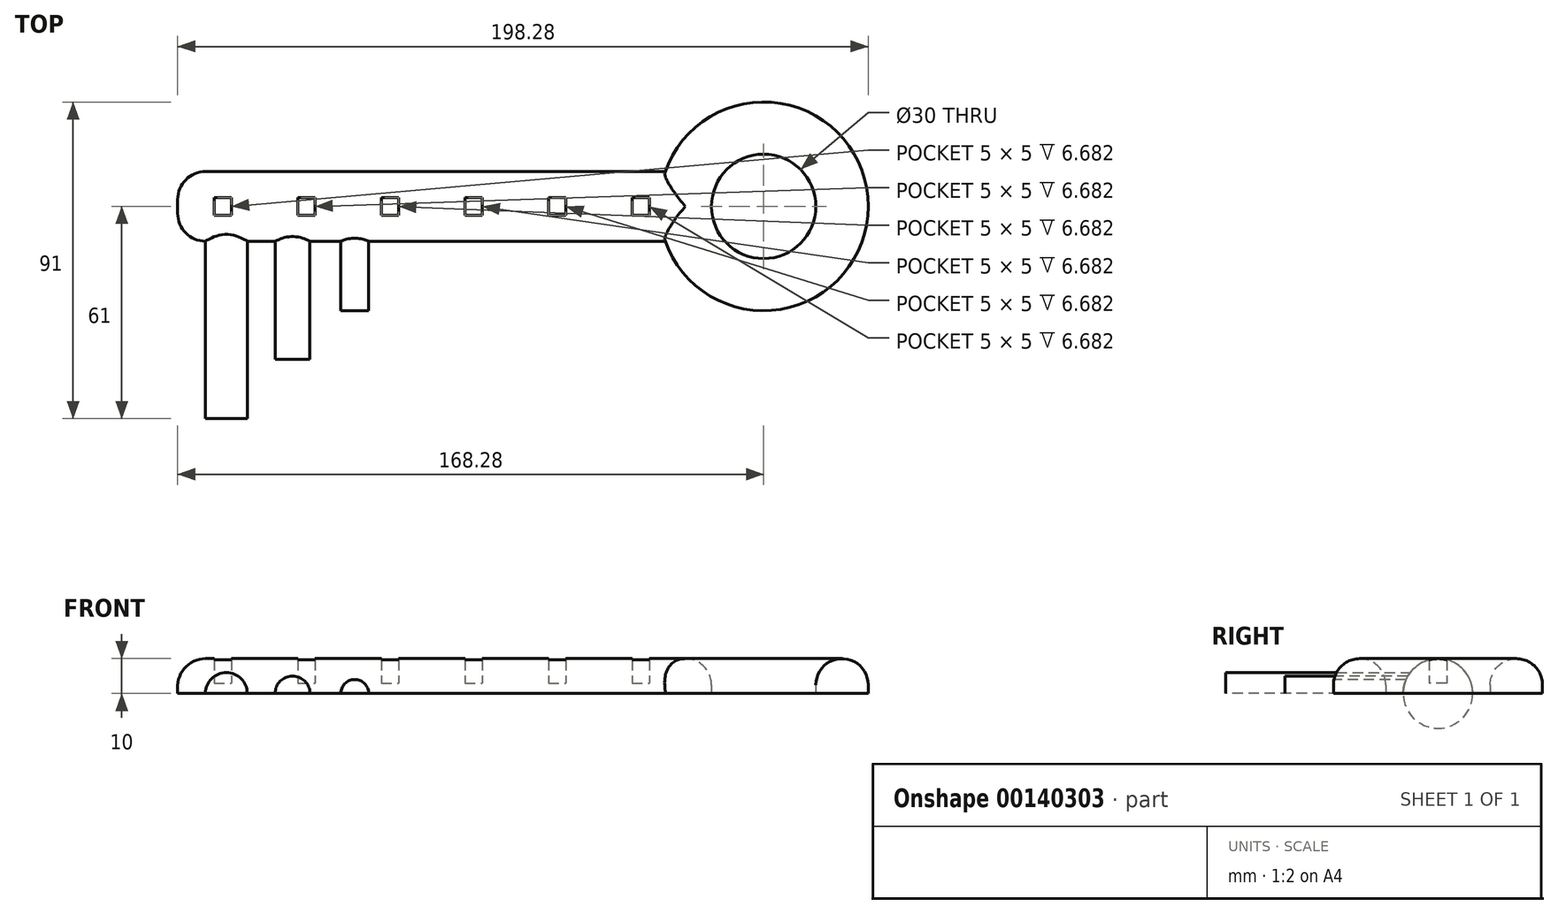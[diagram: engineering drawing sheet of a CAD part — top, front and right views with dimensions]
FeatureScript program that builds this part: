
annotation { "Feature Type Name" : "Feature", "Feature Type Description" : "" }
export const myFeature = defineFeature(function(context is Context, id is Id, definition is map)
    precondition{}
    {
        {
            var Q0;
            Q0=qCreatedBy(makeId("Top.planeOp"),FACE);
            var sketch = newSketch(context, id + "F0", { "sketchPlane" : qUnion([Q0])});
            skCircle(sketch, "E0", {"center": v(155.3, 0) * mm, "radius": 15 * mm});
            skCircle(sketch, "E1", {"center": v(155.3, 0) * mm, "radius": 30 * mm});
            skLineSegment(sketch, "E2", {"start": v(127.02, 10) * mm, "end": v(-12.98, 10) * mm});
            skLineSegment(sketch, "E3", {"start": v(-12.98, 10) * mm, "end": v(-12.98, -10) * mm});
            skPoint(sketch, "E4.first.point", {"position": v(185.3, 0) * mm});
            skLineSegment(sketch, "E5.bottom", {"start": v(-4.98, -10) * mm, "end": v(7.02, -10) * mm});
            skLineSegment(sketch, "E5.top", {"start": v(-4.98, -61) * mm, "end": v(7.02, -61) * mm});
            skLineSegment(sketch, "E5.left", {"start": v(-4.98, -10) * mm, "end": v(-4.98, -61) * mm});
            skLineSegment(sketch, "E5.right", {"start": v(7.02, -10) * mm, "end": v(7.02, -61) * mm});
            skLineSegment(sketch, "E6.bottom", {"start": v(15.02, -10) * mm, "end": v(25.02, -10) * mm});
            skLineSegment(sketch, "E6.top", {"start": v(15.02, -44) * mm, "end": v(25.02, -44) * mm});
            skLineSegment(sketch, "E6.left", {"start": v(15.02, -10) * mm, "end": v(15.02, -44) * mm});
            skLineSegment(sketch, "E6.right", {"start": v(25.02, -10) * mm, "end": v(25.02, -44) * mm});
            skLineSegment(sketch, "E7.bottom", {"start": v(-2.5, 2.5) * mm, "end": v(2.5, 2.5) * mm});
            skLineSegment(sketch, "E7.top", {"start": v(-2.5, -2.5) * mm, "end": v(2.5, -2.5) * mm});
            skLineSegment(sketch, "E7.left", {"start": v(-2.5, 2.5) * mm, "end": v(-2.5, -2.5) * mm});
            skLineSegment(sketch, "E7.right", {"start": v(2.5, 2.5) * mm, "end": v(2.5, -2.5) * mm});
            skPoint(sketch, "E7.middle", {"position": v(0, 0) * mm});
            skLineSegment(sketch, "E8.bottom", {"start": v(21.5, 2.5) * mm, "end": v(26.5, 2.5) * mm});
            skLineSegment(sketch, "E8.top", {"start": v(21.5, -2.5) * mm, "end": v(26.5, -2.5) * mm});
            skLineSegment(sketch, "E8.left", {"start": v(21.5, 2.5) * mm, "end": v(21.5, -2.5) * mm});
            skLineSegment(sketch, "E8.right", {"start": v(26.5, 2.5) * mm, "end": v(26.5, -2.5) * mm});
            skPoint(sketch, "E8.middle", {"position": v(24, 0) * mm});
            skLineSegment(sketch, "E9.bottom", {"start": v(45.5, 2.5) * mm, "end": v(50.5, 2.5) * mm});
            skLineSegment(sketch, "E9.top", {"start": v(45.5, -2.5) * mm, "end": v(50.5, -2.5) * mm});
            skLineSegment(sketch, "E9.left", {"start": v(45.5, 2.5) * mm, "end": v(45.5, -2.5) * mm});
            skLineSegment(sketch, "E9.right", {"start": v(50.5, 2.5) * mm, "end": v(50.5, -2.5) * mm});
            skPoint(sketch, "E9.middle", {"position": v(48, 0) * mm});
            skLineSegment(sketch, "E10.bottom", {"start": v(69.5, 2.5) * mm, "end": v(74.5, 2.5) * mm});
            skLineSegment(sketch, "E10.top", {"start": v(69.5, -2.5) * mm, "end": v(74.5, -2.5) * mm});
            skLineSegment(sketch, "E10.left", {"start": v(69.5, 2.5) * mm, "end": v(69.5, -2.5) * mm});
            skLineSegment(sketch, "E10.right", {"start": v(74.5, 2.5) * mm, "end": v(74.5, -2.5) * mm});
            skPoint(sketch, "E10.middle", {"position": v(72, 0) * mm});
            skLineSegment(sketch, "E11.bottom", {"start": v(93.5, 2.5) * mm, "end": v(98.5, 2.5) * mm});
            skLineSegment(sketch, "E11.top", {"start": v(93.5, -2.5) * mm, "end": v(98.5, -2.5) * mm});
            skLineSegment(sketch, "E11.left", {"start": v(93.5, 2.5) * mm, "end": v(93.5, -2.5) * mm});
            skLineSegment(sketch, "E11.right", {"start": v(98.5, 2.5) * mm, "end": v(98.5, -2.5) * mm});
            skPoint(sketch, "E11.middle", {"position": v(96, 0) * mm});
            skLineSegment(sketch, "E12.bottom", {"start": v(117.5, 2.5) * mm, "end": v(122.5, 2.5) * mm});
            skLineSegment(sketch, "E12.top", {"start": v(117.5, -2.5) * mm, "end": v(122.5, -2.5) * mm});
            skLineSegment(sketch, "E12.left", {"start": v(117.5, 2.5) * mm, "end": v(117.5, -2.5) * mm});
            skLineSegment(sketch, "E12.right", {"start": v(122.5, 2.5) * mm, "end": v(122.5, -2.5) * mm});
            skPoint(sketch, "E12.middle", {"position": v(120, 0) * mm});
            skLineSegment(sketch, "E13", {"start": v(-12.98, -10) * mm, "end": v(-4.98, -10) * mm});
            skLineSegment(sketch, "E14", {"start": v(7.02, -10) * mm, "end": v(15.02, -10) * mm});
            skLineSegment(sketch, "E15", {"start": v(25.02, -10) * mm, "end": v(33.87, -10) * mm});
            skLineSegment(sketch, "E16", {"start": v(33.87, -10) * mm, "end": v(33.87, -30) * mm});
            skLineSegment(sketch, "E17", {"start": v(33.87, -30) * mm, "end": v(41.87, -30) * mm});
            skLineSegment(sketch, "E18", {"start": v(41.87, -30) * mm, "end": v(41.87, -10) * mm});
            skLineSegment(sketch, "E19", {"start": v(41.87, -10) * mm, "end": v(127.02, -10) * mm});
            skLineSegment(sketch, "E20", {"start": v(33.87, -10) * mm, "end": v(41.87, -10) * mm});
            skSolve(sketch);
        }
        {
            var Q0;
            {var subQ5=sQuery(id+"F0.wireOp",EDGE,"E2");Q0=makeQuery(id+"F0.imprint","IMPRINT",FACE,{"disambiguationData":[TD([[makeQuery(id+"F0.imprint","IMPRINT",EDGE,{"derivedFrom":subQ5}),1.0]])]});}
            var Q1;
            Q1=makeQuery(id+"F0.imprint","IMPRINT",FACE,{"disambiguationData":[TD([[makeQuery(id+"F0.imprint","IMPRINT",EDGE,{"derivedFrom":sQuery(id+"F0.wireOp",EDGE,"E0")}),-1.0]])]});
            extrude(context, id + "F1", {"entities" : qUnion([Q0, Q1]), "depth" : 10 * mm});
        }
        {
            var Q0;
            Q0=makeQuery(id+"F0.imprint","IMPRINT",FACE,{"disambiguationData":[TD([[makeQuery(id+"F0.imprint","IMPRINT",EDGE,{"derivedFrom":sQuery(id+"F0.wireOp",EDGE,"E5.bottom")}),-1.0]])]});
            extrude(context, id + "F2", {"entities" : qUnion([Q0]), "operationType" : NewBodyOperationType.ADD, "depth" : 6 * mm});
        }
        {
            var Q0;
            Q0=makeQuery(id+"F0.imprint","IMPRINT",FACE,{"disambiguationData":[TD([[makeQuery(id+"F0.imprint","IMPRINT",EDGE,{"derivedFrom":sQuery(id+"F0.wireOp",EDGE,"E6.bottom")}),-1.0]])]});
            extrude(context, id + "F3", {"entities" : qUnion([Q0]), "operationType" : NewBodyOperationType.ADD, "depth" : 5 * mm});
        }
        {
            var Q0;
            Q0=makeQuery(id+"F0.imprint","IMPRINT",FACE,{"disambiguationData":[TD([[makeQuery(id+"F0.imprint","IMPRINT",EDGE,{"derivedFrom":sQuery(id+"F0.wireOp",EDGE,"E16")}),1.0]])]});
            extrude(context, id + "F4", {"entities" : qUnion([Q0]), "operationType" : NewBodyOperationType.ADD, "depth" : 4 * mm});
        }
        {
            var Q0;
            Q0=makeQuery(id+"F1.opExtrude","CAP_EDGE",EDGE,{"disambiguationData":[OSD([sQuery(id+"F0.wireOp",EDGE,"E1")])],"isStart":false});
            var Q1;
            Q1=makeQuery(id+"F1.opExtrude","CAP_EDGE",EDGE,{"disambiguationData":[OSD([sQuery(id+"F0.wireOp",EDGE,"E0")])],"isStart":false});
            fillet(context, id + "F5", {"entities" : qUnion([Q0, Q1]), "radius" : 7.5 * mm, "tangentPropagation" : true, "allowEdgeOverflow" : false});
        }
        {
            var Q0;
            Q0=makeQuery(id+"F2.opExtrude","CAP_EDGE",EDGE,{"disambiguationData":[OSD([sQuery(id+"F0.wireOp",EDGE,"E5.left")])],"isStart":false});
            var Q1;
            Q1=makeQuery(id+"F2.opExtrude","CAP_EDGE",EDGE,{"disambiguationData":[OSD([sQuery(id+"F0.wireOp",EDGE,"E5.right")])],"isStart":false});
            fillet(context, id + "F6", {"entities" : qUnion([Q0, Q1]), "radius" : 6 * mm, "tangentPropagation" : true, "allowEdgeOverflow" : false});
        }
        {
            var Q0;
            Q0=makeQuery(id+"F3.opExtrude","CAP_EDGE",EDGE,{"disambiguationData":[OSD([sQuery(id+"F0.wireOp",EDGE,"E6.right")])],"isStart":false});
            var Q1;
            Q1=makeQuery(id+"F3.opExtrude","CAP_EDGE",EDGE,{"disambiguationData":[OSD([sQuery(id+"F0.wireOp",EDGE,"E6.left")])],"isStart":false});
            fillet(context, id + "F7", {"entities" : qUnion([Q0, Q1]), "radius" : 5 * mm, "tangentPropagation" : true, "allowEdgeOverflow" : false});
        }
        {
            var Q0;
            Q0=makeQuery(id+"F4.opExtrude","CAP_EDGE",EDGE,{"disambiguationData":[OSD([sQuery(id+"F0.wireOp",EDGE,"E18")])],"isStart":false});
            var Q1;
            Q1=makeQuery(id+"F4.opExtrude","CAP_EDGE",EDGE,{"disambiguationData":[OSD([sQuery(id+"F0.wireOp",EDGE,"E16")])],"isStart":false});
            fillet(context, id + "F8", {"entities" : qUnion([Q0, Q1]), "radius" : 4 * mm, "tangentPropagation" : true, "allowEdgeOverflow" : false});
        }
        {
            var Q0;
            Q0=makeQuery(id+"F0.imprint","IMPRINT",FACE,{"disambiguationData":[TD([[makeQuery(id+"F0.imprint","IMPRINT",EDGE,{"derivedFrom":sQuery(id+"F0.wireOp",EDGE,"E7.bottom")}),-1.0]])]});
            var Q1;
            Q1=makeQuery(id+"F0.imprint","IMPRINT",FACE,{"disambiguationData":[TD([[makeQuery(id+"F0.imprint","IMPRINT",EDGE,{"derivedFrom":sQuery(id+"F0.wireOp",EDGE,"E8.bottom")}),-1.0]])]});
            var Q2;
            Q2=makeQuery(id+"F0.imprint","IMPRINT",FACE,{"disambiguationData":[TD([[makeQuery(id+"F0.imprint","IMPRINT",EDGE,{"derivedFrom":sQuery(id+"F0.wireOp",EDGE,"E9.bottom")}),-1.0]])]});
            var Q3;
            Q3=makeQuery(id+"F0.imprint","IMPRINT",FACE,{"disambiguationData":[TD([[makeQuery(id+"F0.imprint","IMPRINT",EDGE,{"derivedFrom":sQuery(id+"F0.wireOp",EDGE,"E10.bottom")}),-1.0]])]});
            var Q4;
            Q4=makeQuery(id+"F0.imprint","IMPRINT",FACE,{"disambiguationData":[TD([[makeQuery(id+"F0.imprint","IMPRINT",EDGE,{"derivedFrom":sQuery(id+"F0.wireOp",EDGE,"E11.bottom")}),-1.0]])]});
            var Q5;
            Q5=makeQuery(id+"F0.imprint","IMPRINT",FACE,{"disambiguationData":[TD([[makeQuery(id+"F0.imprint","IMPRINT",EDGE,{"derivedFrom":sQuery(id+"F0.wireOp",EDGE,"E12.bottom")}),-1.0]])]});
            extrude(context, id + "F9", {"entities" : qUnion([Q0, Q1, Q2, Q3, Q4, Q5]), "operationType" : NewBodyOperationType.ADD, "depth" : 3 * mm});
        }
        {
            var Q0;
            Q0=makeQuery(id+"F1.opExtrude","CAP_EDGE",EDGE,{"disambiguationData":[OSD([sQuery(id+"F0.wireOp",EDGE,"E2")])],"isStart":false});
            var Q1;
            Q1=makeQuery(id+"F1.opExtrude","CAP_EDGE",EDGE,{"disambiguationData":[OSD([sQuery(id+"F0.wireOp",EDGE,"E5.bottom"),sQuery(id+"F0.wireOp",EDGE,"E6.bottom"),sQuery(id+"F0.wireOp",EDGE,"E13"),sQuery(id+"F0.wireOp",EDGE,"E14"),sQuery(id+"F0.wireOp",EDGE,"E15"),sQuery(id+"F0.wireOp",EDGE,"E19"),sQuery(id+"F0.wireOp",EDGE,"E20")])],"isStart":false});
            fillet(context, id + "F10", {"entities" : qUnion([Q0, Q1]), "radius" : 10 * mm, "tangentPropagation" : true, "allowEdgeOverflow" : false});
        }
        {
            var Q0;
            Q0=makeQuery(id+"F10.opFillet","BLEND_EDGE",EDGE,{"blendedFrom":[makeQuery(id+"F1.opExtrude","CAP_EDGE",EDGE,{"disambiguationData":[OSD([sQuery(id+"F0.wireOp",EDGE,"E2")])],"isStart":false}),makeQuery(id+"F1.opExtrude","SWEPT_FACE",FACE,{"disambiguationData":[OSD([sQuery(id+"F0.wireOp",EDGE,"E3")])]})],"blendedInto":[makeQuery(id+"F1.opExtrude","SWEPT_FACE",FACE,{"disambiguationData":[OSD([sQuery(id+"F0.wireOp",EDGE,"E3")])]})]});
            fillet(context, id + "F11", {"entities" : qUnion([Q0]), "radius" : 8 * mm, "tangentPropagation" : true, "allowEdgeOverflow" : false});
        }
    });
